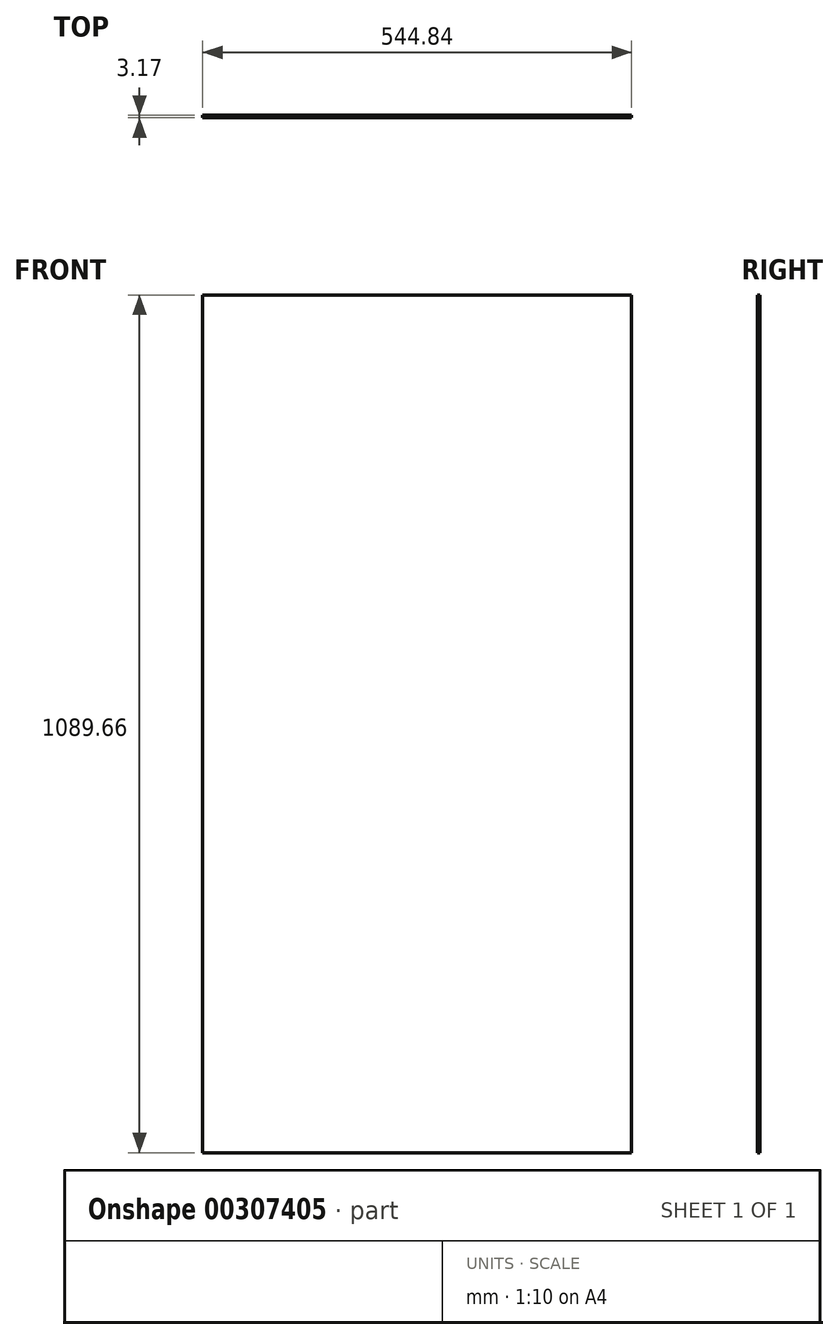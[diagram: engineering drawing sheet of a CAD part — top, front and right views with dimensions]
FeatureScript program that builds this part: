
annotation { "Feature Type Name" : "Feature", "Feature Type Description" : "" }
export const myFeature = defineFeature(function(context is Context, id is Id, definition is map)
    precondition{}
    {
        {
            var Q0;
            Q0=qCreatedBy(makeId("Front.planeOp"),FACE);
            var sketch = newSketch(context, id + "F0", { "sketchPlane" : qUnion([Q0])});
            skLineSegment(sketch, "E0.bottom", {"start": v(272.42, 544.83) * mm, "end": v(-272.42, 544.83) * mm});
            skLineSegment(sketch, "E0.top", {"start": v(272.42, -544.83) * mm, "end": v(-272.42, -544.83) * mm});
            skLineSegment(sketch, "E0.left", {"start": v(272.42, 544.83) * mm, "end": v(272.42, -544.83) * mm});
            skLineSegment(sketch, "E0.right", {"start": v(-272.42, 544.83) * mm, "end": v(-272.42, -544.83) * mm});
            skPoint(sketch, "E0.middle", {"position": v(0, 0) * mm});
            skSolve(sketch);
        }
        {
            var Q0;
            Q0 = qSketchRegion(id + "F0", true);
            extrude(context, id + "F1", {"entities" : qUnion([Q0]), "depth" : 3.17 * mm});
        }
    });
